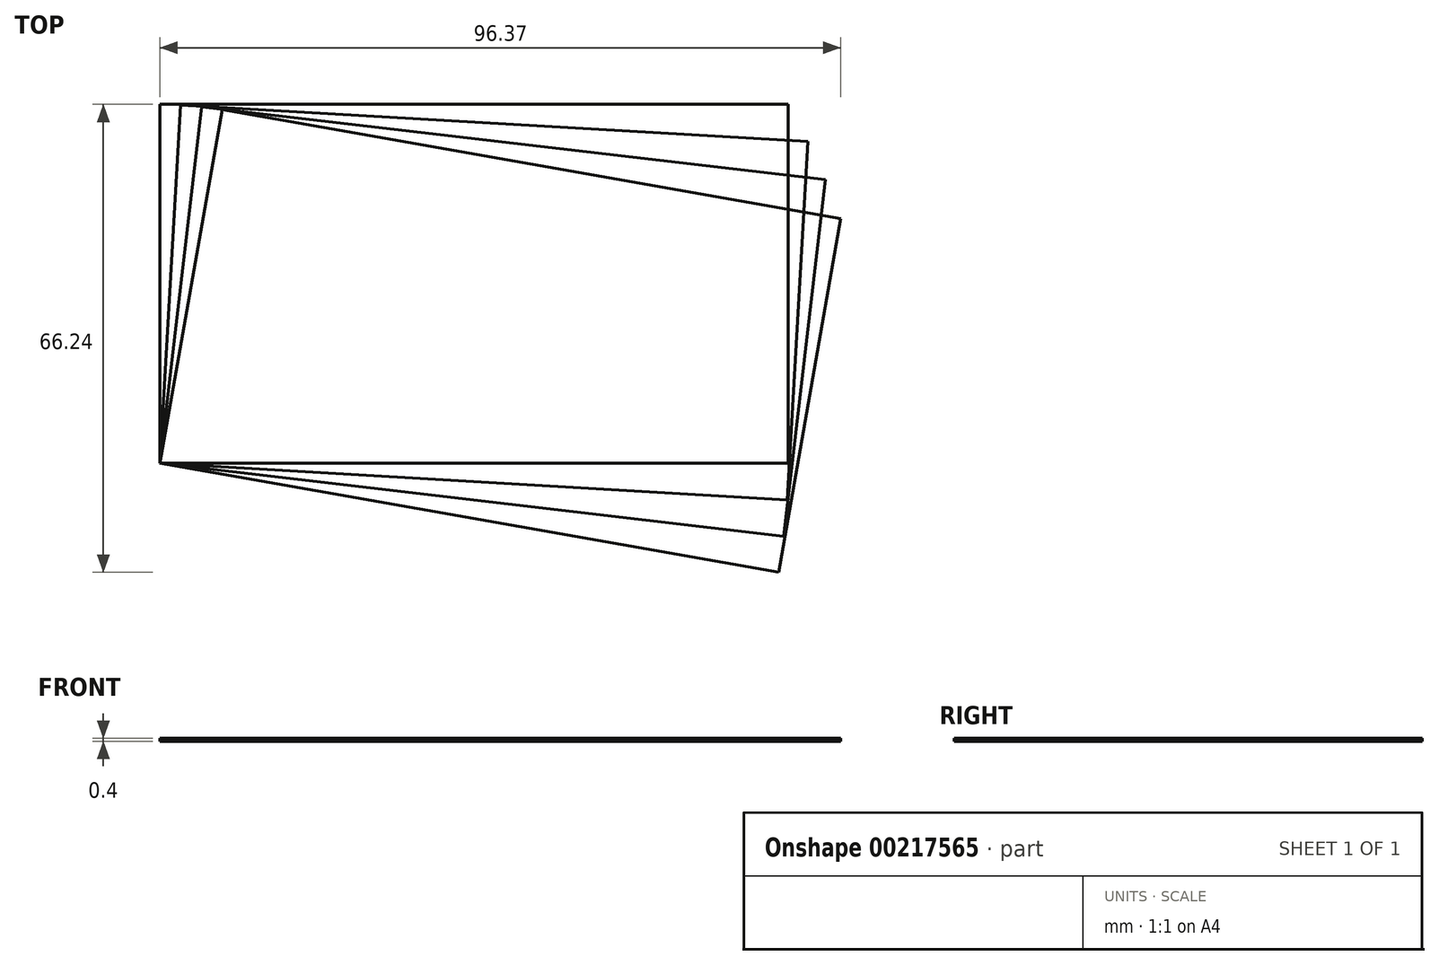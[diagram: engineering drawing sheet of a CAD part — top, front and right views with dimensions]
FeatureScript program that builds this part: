
annotation { "Feature Type Name" : "Feature", "Feature Type Description" : "" }
export const myFeature = defineFeature(function(context is Context, id is Id, definition is map)
    precondition{}
    {
        {
            var Q0;
            Q0=qCreatedBy(makeId("Top.planeOp"),FACE);
            var sketch = newSketch(context, id + "F0", { "sketchPlane" : qUnion([Q0])});
            skLineSegment(sketch, "E0.bottom", {"start": v(-44.45, 25.4) * mm, "end": v(44.45, 25.4) * mm});
            skLineSegment(sketch, "E0.top", {"start": v(-44.45, -25.4) * mm, "end": v(44.45, -25.4) * mm});
            skLineSegment(sketch, "E0.left", {"start": v(-44.45, 25.4) * mm, "end": v(-44.45, -25.4) * mm});
            skLineSegment(sketch, "E0.right", {"start": v(44.45, 25.4) * mm, "end": v(44.45, -25.4) * mm});
            skPoint(sketch, "E0.middle", {"position": v(0, 0) * mm});
            skSolve(sketch);
        }
        {
            var Q0;
            Q0 = qSketchRegion(id + "F0", true);
            extrude(context, id + "F1", {"entities" : qUnion([Q0]), "depth" : .4 * mm});
        }
        {
            var Q0;
            Q0=makeQuery(id+"F1.opExtrude","SWEPT_BODY",BODY,{"disambiguationData":[OSD([sQuery(id+"F0.wireOp",EDGE,"E0.bottom"),sQuery(id+"F0.wireOp",EDGE,"E0.top"),sQuery(id+"F0.wireOp",EDGE,"E0.left"),sQuery(id+"F0.wireOp",EDGE,"E0.right")])]});
            var Q1;
            Q1=makeQuery(id+"F1.opExtrude","SWEPT_EDGE",EDGE,{"disambiguationData":[OSD([sQuery(id+"F0.wireOp",EDGE,"E0.top"),sQuery(id+"F0.wireOp",EDGE,"E0.left")])]});
            circularPattern(context, id + "F2", {"entities" : qUnion([Q0]), "axis" : qUnion([Q1]), "angle" : 10 * degree, "instanceCount" : 4, "equalSpace" : true});
        }
    });
